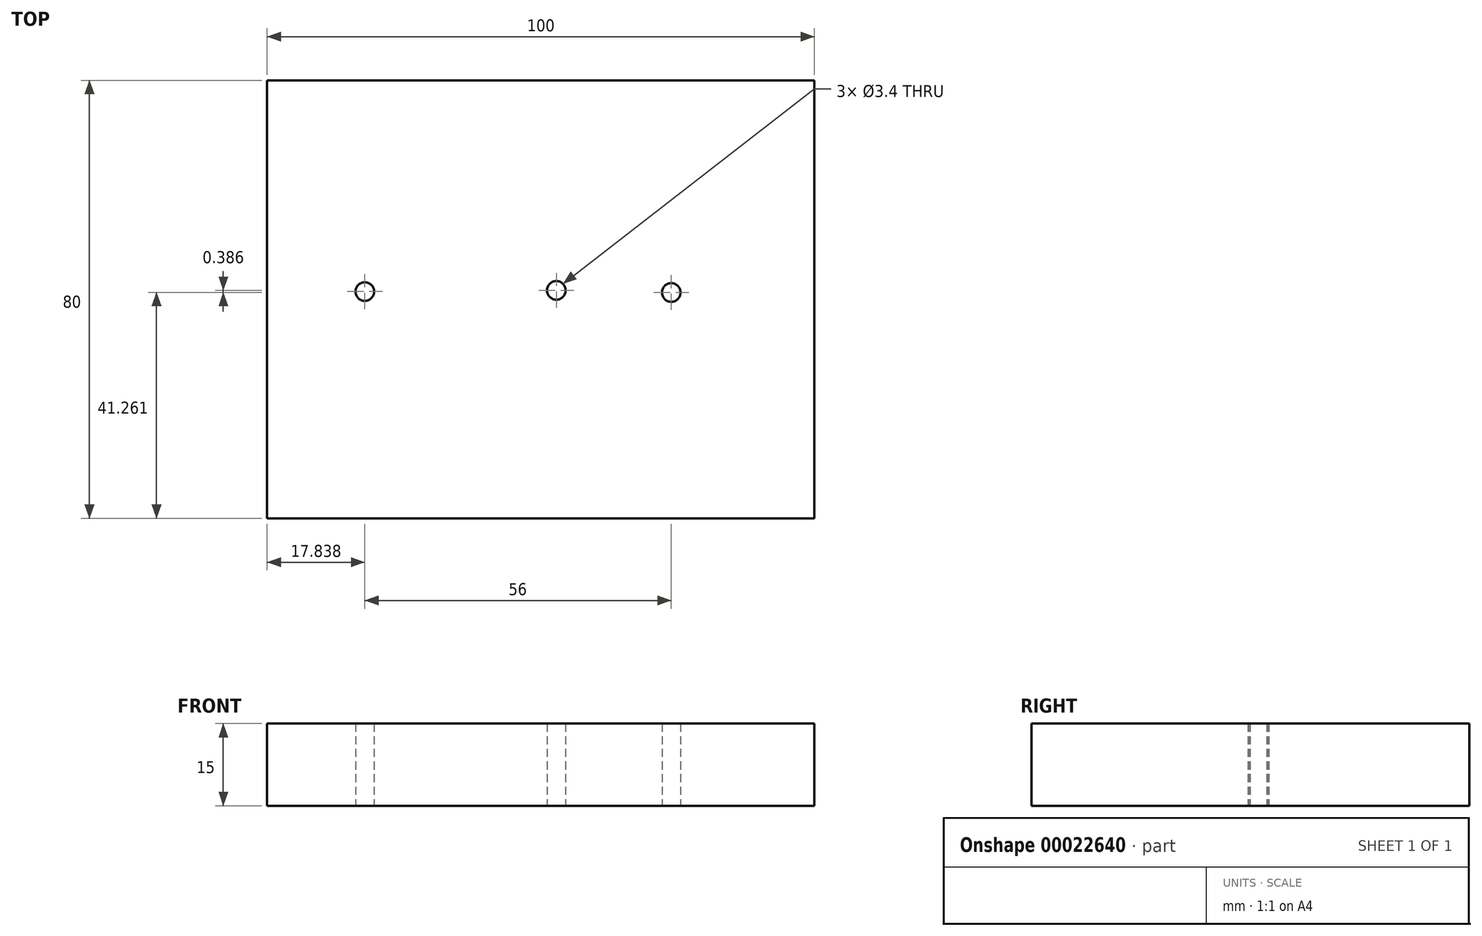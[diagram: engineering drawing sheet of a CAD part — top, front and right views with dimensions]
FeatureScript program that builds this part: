
annotation { "Feature Type Name" : "Feature", "Feature Type Description" : "" }
export const myFeature = defineFeature(function(context is Context, id is Id, definition is map)
    precondition{}
    {
        {
            var Q0;
            Q0=qCreatedBy(makeId("Top.planeOp"),FACE);
            var sketch = newSketch(context, id + "F0", { "sketchPlane" : qUnion([Q0])});
            skLineSegment(sketch, "E0.bottom", {"start": v(-73.54, 38.57) * mm, "end": v(26.46, 38.57) * mm});
            skLineSegment(sketch, "E0.top", {"start": v(-73.54, -41.43) * mm, "end": v(26.46, -41.43) * mm});
            skLineSegment(sketch, "E0.left", {"start": v(-73.54, 38.57) * mm, "end": v(-73.54, -41.43) * mm});
            skLineSegment(sketch, "E0.right", {"start": v(26.46, 38.57) * mm, "end": v(26.46, -41.43) * mm});
            skCircle(sketch, "E1", {"center": v(-55.7, 0) * mm, "radius": 1.7 * mm});
            skCircle(sketch, "E2", {"center": v(-20.7, 0.22) * mm, "radius": 1.7 * mm});
            skCircle(sketch, "E3", {"center": v(0.3, -0.17) * mm, "radius": 1.7 * mm});
            skSolve(sketch);
        }
        {
            var Q0;
            Q0=makeQuery(id+"F0.imprint","IMPRINT",FACE,{"disambiguationData":[TD([[makeQuery(id+"F0.imprint","IMPRINT",EDGE,{"derivedFrom":sQuery(id+"F0.wireOp",EDGE,"E0.bottom")}),-1.0]])]});
            extrude(context, id + "F1", {"entities" : qUnion([Q0]), "depth" : 15 * mm});
        }
    });
